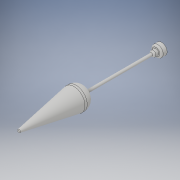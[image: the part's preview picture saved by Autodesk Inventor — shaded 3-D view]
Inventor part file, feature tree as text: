
AUTODESK INVENTOR PART (.ipt)
format: ipt  version: 2017 (Build 210142000, 142)  size: 154,624 bytes
history: native  units: in
note: dims shown in document units (in); Inventor stores cm internally (conversion verified against a paired STEP export)
features: extrude x5, sketch x4, fillet x3, other x2, thicken_offset x1, loft x1
ambient origin geometry x8: Origin, YZ Plane, XZ Plane, XY Plane, X Axis, Y Axis, Z Axis, Center Point
bodies: Solid1 (feature_tree)
feature tree (16):
  sketch  "Sketch1"  dims[d0=0.5in d1=0.25in]
  extrude  "Extrusion1"  Depth=0.25in
  extrude  "Extrusion2"  Depth=0.45in TaperAngle=0.0deg
  extrude  "Extrusion3"  Depth=3.0in TaperAngle=0.0deg
  extrude  "Extrusion6"  Depth=3.0in TaperAngle=0.0deg
  fillet  "Fillet3"  Radius=0.4in
  thicken_offset  "Thicken1"
  extrude  "Extrusion13"  Depth=2.5in
  loft  "Loft1"
  fillet  "Fillet5"  Radius=2.5in
  fillet  "Fillet6"  [1 undecoded]
  sketch  "Sketch2"  dims[d2=0.25in d3=0.0in d4=0.45in d5=0.0in]
  sketch  "Sketch5"  dims[d7=0.125in d8=3.0in d9=0.0in]
  sketch  "Sketch14"  dims[d16=1.0in d17=3.0in d18=0.0in d19=0.4in d20=2.5in d21=2.5in d41=2.5in d42=0.0in d43=0.0in d44=90.0deg d45=0.0in d46=90.0deg d47=0.075in d48=0.035in]
  other  "Edges1"
  other  "Edges2"
note: 1 required parameter value undecoded (feature->parameter linkage not recoverable at this tier; creation-order binding heuristic only, values carry confidence <= 0.55)
